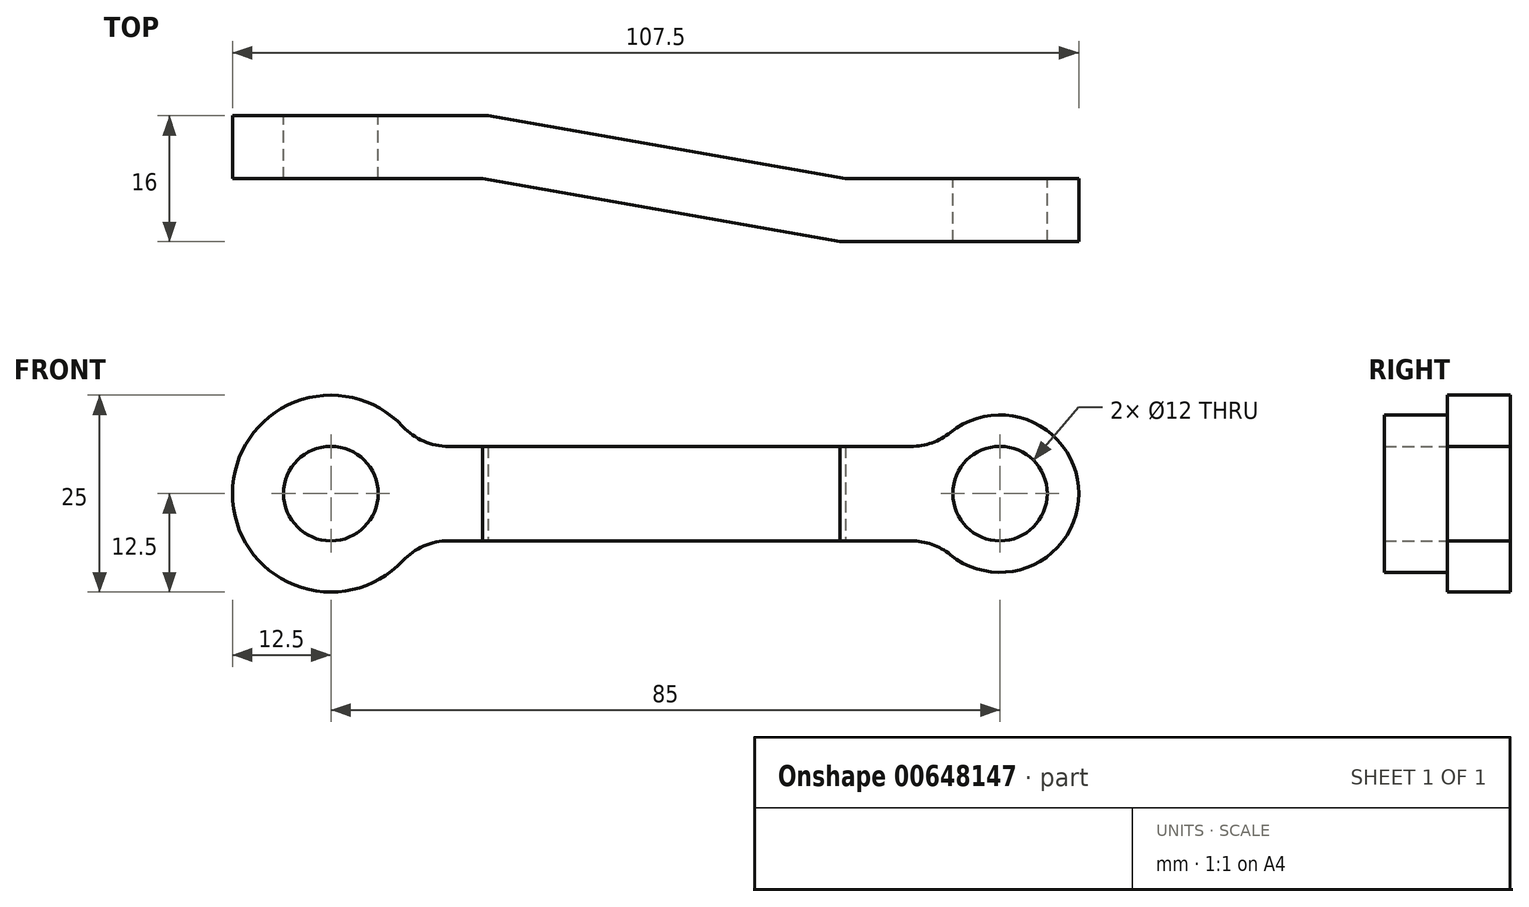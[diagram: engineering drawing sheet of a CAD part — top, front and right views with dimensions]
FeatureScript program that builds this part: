
annotation { "Feature Type Name" : "Feature", "Feature Type Description" : "" }
export const myFeature = defineFeature(function(context is Context, id is Id, definition is map)
    precondition{}
    {
        {
            var Q0;
            Q0=qCreatedBy(makeId("Front.planeOp"),FACE);
            var sketch = newSketch(context, id + "F0", { "sketchPlane" : qUnion([Q0])});
            skCircle(sketch, "E0", {"center": v(0, 0) * mm, "radius": 12.5 * mm});
            skCircle(sketch, "E1", {"center": v(85, 0) * mm, "radius": 10 * mm});
            skLineSegment(sketch, "E2", {"start": v(0, 0) * mm, "end": v(85, 0) * mm, "construction": true});
            skLineSegment(sketch, "E3", {"start": v(10.97, 6) * mm, "end": v(77, 6) * mm});
            skLineSegment(sketch, "E4.MirrorCS", {"start": v(10.97, -6) * mm, "end": v(77, -6) * mm});
            skCircle(sketch, "E5", {"center": v(0, 0) * mm, "radius": 6 * mm});
            skCircle(sketch, "E6", {"center": v(85, 0) * mm, "radius": 6 * mm});
            skSolve(sketch);
        }
        {
            var Q0;
            Q0=makeQuery(id+"F0.imprint","IMPRINT",FACE,{"disambiguationData":[TD([[makeQuery(id+"F0.imprint","IMPRINT",EDGE,{"derivedFrom":sQuery(id+"F0.wireOp",EDGE,"E5")}),-1.0]])]});
            var Q1;
            {var subQ0=sQuery(id+"F0.wireOp",EDGE,"E3");Q1=makeQuery(id+"F0.imprint","IMPRINT",FACE,{"disambiguationData":[TD([[makeQuery(id+"F0.imprint","IMPRINT",EDGE,{"derivedFrom":subQ0}),-1.0]])]});}
            var Q2;
            Q2=makeQuery(id+"F0.imprint","IMPRINT",FACE,{"disambiguationData":[TD([[makeQuery(id+"F0.imprint","IMPRINT",EDGE,{"derivedFrom":sQuery(id+"F0.wireOp",EDGE,"E6")}),-1.0]])]});
            extrude(context, id + "F1", {"entities" : qUnion([Q0, Q1, Q2]), "depth" : 25 * mm, "offsetDistance" : 25 * mm});
        }
        {
            var Q0;
            Q0=qCreatedBy(makeId("Top.planeOp"),FACE);
            var sketch = newSketch(context, id + "F2", { "sketchPlane" : qUnion([Q0])});
            skLineSegment(sketch, "E7", {"start": v(-12.5, 0) * mm, "end": v(20, 0) * mm});
            skLineSegment(sketch, "E8", {"start": v(20, 0) * mm, "end": v(65.37, -8) * mm});
            skLineSegment(sketch, "E9", {"start": v(65.37, -8) * mm, "end": v(95, -8) * mm});
            skLineSegment(sketch, "E10.0", {"start": v(64.67, -16) * mm, "end": v(95, -16) * mm});
            skLineSegment(sketch, "E10.1", {"start": v(19.3, -8) * mm, "end": v(64.67, -16) * mm});
            skLineSegment(sketch, "E10.2", {"start": v(-12.5, -8) * mm, "end": v(19.3, -8) * mm});
            skLineSegment(sketch, "E11", {"start": v(95, 0) * mm, "end": v(95, -25) * mm});
            skLineSegment(sketch, "E12", {"start": v(-12.5, -25) * mm, "end": v(-12.5, 0) * mm});
            skLineSegment(sketch, "E13", {"start": v(-12.5, -8) * mm, "end": v(-12.5, 0) * mm});
            skLineSegment(sketch, "E14", {"start": v(95, -16) * mm, "end": v(95, -8) * mm});
            skSolve(sketch);
        }
        {
            var Q0;
            Q0 = qSketchRegion(id + "F2", true);
            extrude(context, id + "F3", {"entities" : qUnion([Q0]), "operationType" : NewBodyOperationType.INTERSECT, "endBound" : BoundingType.SYMMETRIC, "depth" : 25 * mm, "offsetDistance" : 25 * mm});
        }
        {
            var Q0;
            Q0=makeQuery(id+"F1.opExtrude","SWEPT_EDGE",EDGE,{"disambiguationData":[OSD([sQuery(id+"F0.wireOp",EDGE,"E0"),sQuery(id+"F0.wireOp",EDGE,"E4.MirrorCS")])]});
            var Q1;
            Q1=makeQuery(id+"F1.opExtrude","SWEPT_EDGE",EDGE,{"disambiguationData":[OSD([sQuery(id+"F0.wireOp",EDGE,"E0"),sQuery(id+"F0.wireOp",EDGE,"E3")])]});
            var Q2;
            Q2=makeQuery(id+"F1.opExtrude","SWEPT_EDGE",EDGE,{"disambiguationData":[OSD([sQuery(id+"F0.wireOp",EDGE,"E1"),sQuery(id+"F0.wireOp",EDGE,"E3")])]});
            var Q3;
            Q3=makeQuery(id+"F1.opExtrude","SWEPT_EDGE",EDGE,{"disambiguationData":[OSD([sQuery(id+"F0.wireOp",EDGE,"E1"),sQuery(id+"F0.wireOp",EDGE,"E4.MirrorCS")])]});
            fillet(context, id + "F4", {"entities" : qUnion([Q0, Q1, Q2, Q3]), "tangentPropagation" : true, "radius" : 8 * mm, "defaultsChanged" : true, "vertexSettings" : [], "allowEdgeOverflow" : false});
        }
    });
